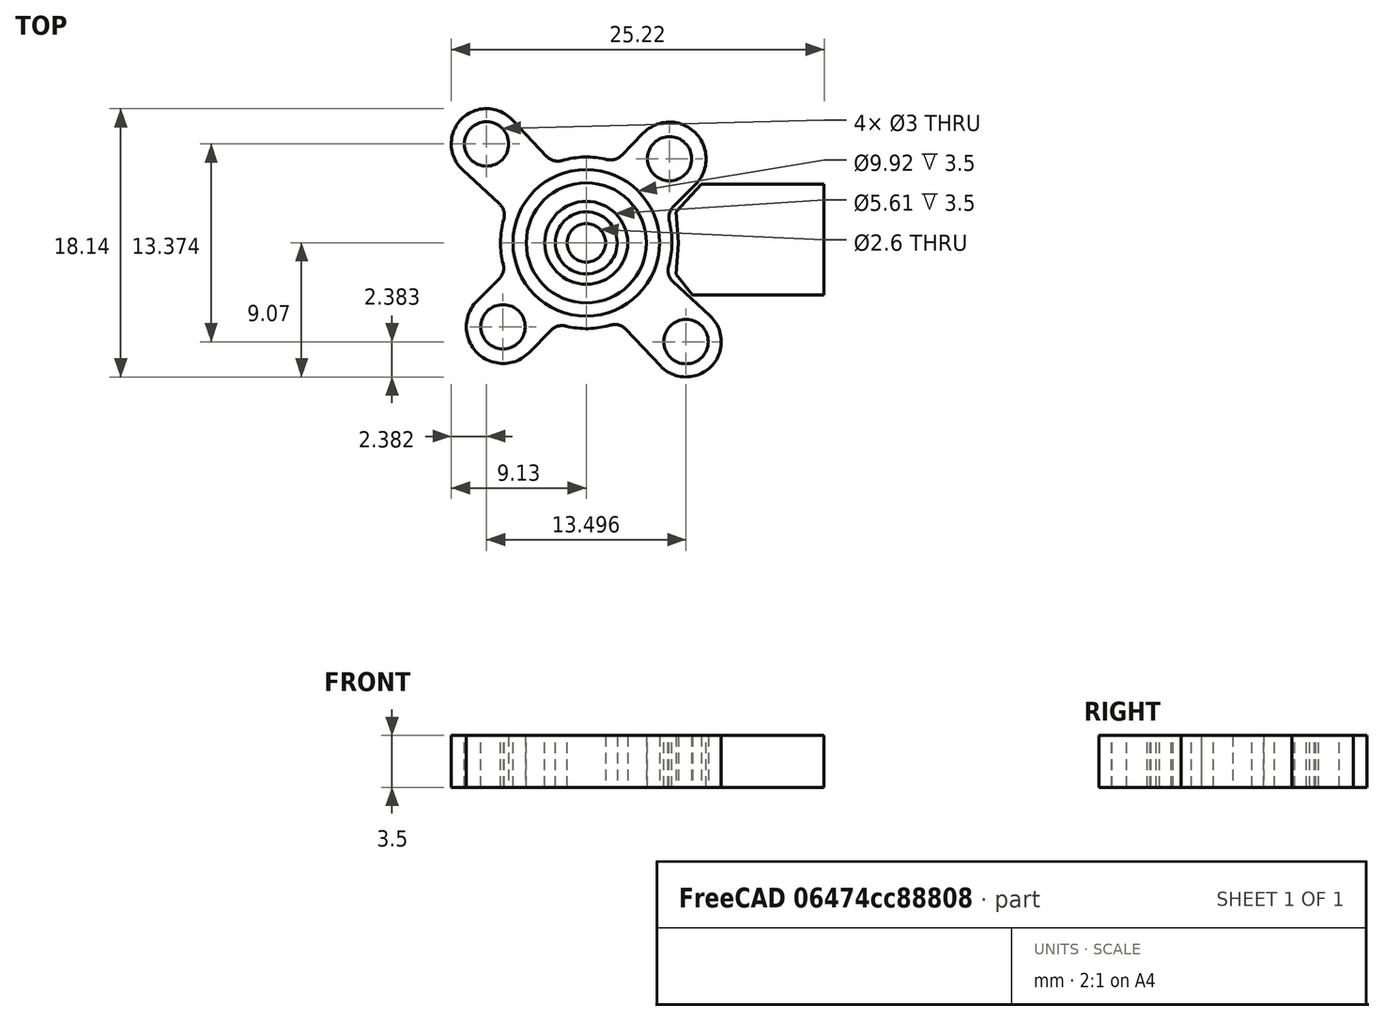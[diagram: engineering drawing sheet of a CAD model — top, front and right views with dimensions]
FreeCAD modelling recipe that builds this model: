
FCSTD DOCUMENT  (FreeCAD 0.18RUnknown)
Label: r6_bottom
License: All rights reserved
LicenseURL: http://en.wikipedia.org/wiki/All_rights_reserved
objects: Sketcher::SketchObject×2, Part::Extrusion×1
note: 3 computed .brp shape members not serialized (recipe doc carries the construction recipe); baked Part::Feature solids carry a one-line shape summary decoded from their .brp

FEATURE [Sketcher::SketchObject] Sketch  label="body"
  Placement = pos=(0,0,0) rot=(1,0,0;1.5708rad)
  sketch-geometry (23):
    g0: LineSegment StartX=-14 StartY=0 StartZ=0 EndX=14 EndY=0 EndZ=0
    g1: LineSegment StartX=14 StartY=0 StartZ=0 EndX=14 EndY=7.7 EndZ=0
    g2: LineSegment StartX=14 StartY=7.7 StartZ=0 EndX=-14 EndY=7.7 EndZ=0
    g3: LineSegment StartX=-14 StartY=0 StartZ=0 EndX=-14 EndY=7.7 EndZ=0
    g4: LineSegment StartX=-5.833 StartY=13.25 StartZ=0 EndX=5.833 EndY=13.25 EndZ=0
    g5: LineSegment StartX=-2.5 StartY=13.25 StartZ=0 EndX=-2.5 EndY=18.25 EndZ=0
    g6: LineSegment StartX=-2.5 StartY=18.25 StartZ=0 EndX=2.5 EndY=18.25 EndZ=0
    g7: LineSegment StartX=2.5 StartY=18.25 StartZ=0 EndX=2.5 EndY=13.25 EndZ=0
    g8: LineSegment StartX=-2.5 StartY=18.25 StartZ=0 EndX=-2.5 EndY=25.25 EndZ=0
    g9: LineSegment StartX=-2.5 StartY=25.25 StartZ=0 EndX=2.5 EndY=25.25 EndZ=0
    g10: LineSegment StartX=2.5 StartY=25.25 StartZ=0 EndX=2.5 EndY=18.25 EndZ=0
    g11: LineSegment StartX=-5.175 StartY=0 StartZ=0 EndX=-5.75 EndY=-2 EndZ=0
    g12: LineSegment StartX=5.175 StartY=0 StartZ=0 EndX=5.75 EndY=-2 EndZ=0
    g13: LineSegment StartX=-5.75 StartY=-2 StartZ=0 EndX=5.75 EndY=-2 EndZ=0
    g14: GeomPoint X=0 Y=-5.45 Z=0
    g15: GeomPoint X=0 Y=25.25 Z=0
    g16: GeomPoint X=0 Y=13.25 Z=0
    g17: GeomPoint X=10.0114 Y=8.91857 Z=0
    g18: LineSegment StartX=14 StartY=7.7 StartZ=0 EndX=14 EndY=9.64 EndZ=0
    g19: LineSegment StartX=14 StartY=9.64 StartZ=0 EndX=5.833 EndY=13.25 EndZ=0
    g20: LineSegment StartX=-5.833 StartY=13.25 StartZ=0 EndX=-14 EndY=9.64 EndZ=0
    g21: LineSegment StartX=-14 StartY=7.7 StartZ=0 EndX=-14 EndY=9.64 EndZ=0
    g22: GeomPoint X=0 Y=7.7 Z=0
  constraints (62):
    c: PointOnObject(g0,g-1)
    c: Horizontal(g0)
    c: Vertical(g1)
    c: Horizontal(g2)
    c: Coincident(g3,g0)
    c: Coincident(g3,g2)
    c: Vertical(g3)
    c: Horizontal(g4)
    c: PointOnObject(g5,g4)
    c: Vertical(g5)
    c: Coincident(g6,g5)
    c: Horizontal(g6)
    c: Coincident(g7,g6)
    c: PointOnObject(g7,g4)
    c: Vertical(g7)
    c: Coincident(g8,g5)
    c: Vertical(g8)
    c: Horizontal(g9)
    c: Coincident(g10,g9)
    c: Coincident(g10,g6)
    c: Vertical(g10)
    c: PointOnObject(g11,g0)
    c: PointOnObject(g12,g0)
    c: Coincident(g13,g11)
    c: Horizontal(g13)
    c: Coincident(g12,g13)
    c: Coincident(g2,g1)
    c: DistanceY(g11,g11) = 2
    c: PointOnObject(g14,g-2)
    c: Equal(g11,g12)
    c: PointOnObject(g15,g9)
    c: PointOnObject(g16,g4)
    c: PointOnObject(g16,g-2)
    c: PointOnObject(g15,g-2)
    c: Coincident(g9,g8)
    c: DistanceY(g14,g16) = 18.7
    c: Coincident(g0,g1)
    c: DistanceY(g14,g15) = 30.7
    c: DistanceX(g8,g9) = 5
    c: DistanceY(g5,g8) = 7
    c: Symmetric(g8,g9,g-2)
    c: Symmetric(g4,g4,g-2)
    c: DistanceX(g2,g1) = 28
    c: Symmetric(g2,g1,g-2)
    c: DistanceY(g0,g1) = 7.7
    c: Coincident(g18,g1)
    c: Coincident(g19,g18)
    c: Coincident(g19,g4)
    c: Coincident(g20,g4)
    c: Coincident(g21,g2)
    c: Coincident(g21,g20)
    c: Vertical(g18)
    c: Equal(g18,g21)
    c: Equal(g19,g20)
    c: PointOnObject(g22,g2)
    c: PointOnObject(g22,g-2)
    c: DistanceY(g22,g16) = 5.55
    c: Symmetric(g11,g12,g-2)
    c: DistanceX(g11,g12) = 10.35
    c: DistanceY(g1,g18) = 1.94
    c: DistanceX(g11,g12) = 11.5
    c: DistanceX(g4,g4) = 11.666
FEATURE [Sketcher::SketchObject] Sketch001  label="base"
  sketch-geometry (51):
    g0: Circle CenterX=0 CenterY=0 CenterZ=0 NormalX=0 NormalY=0 NormalZ=1 AngleXU=0 Radius=4.95833
    g1: Circle CenterX=0 CenterY=0 CenterZ=0 NormalX=0 NormalY=0 NormalZ=1 AngleXU=0 Radius=4.05855
    g2: Circle CenterX=0 CenterY=0 CenterZ=0 NormalX=0 NormalY=0 NormalZ=1 AngleXU=0 Radius=2.80253
    g3: Circle CenterX=0 CenterY=0 CenterZ=0 NormalX=0 NormalY=0 NormalZ=1 AngleXU=0 Radius=2.09587
    g4: Circle CenterX=0 CenterY=0 CenterZ=0 NormalX=0 NormalY=0 NormalZ=1 AngleXU=0 Radius=1.30129
    g5: ArcOfCircle CenterX=6.748 CenterY=6.68689 CenterZ=0 NormalX=0 NormalY=0 NormalZ=1 AngleXU=0 Radius=2.38428 StartAngle=5.45879 EndAngle=8.66928
    g6: ArcOfCircle CenterX=5.63107 CenterY=-5.68252 CenterZ=0 NormalX=0 NormalY=0 NormalZ=1 AngleXU=0 Radius=2.47766 StartAngle=3.91796 EndAngle=7.06852
    g7: ArcOfCircle CenterX=-6.748 CenterY=-6.68689 CenterZ=0 NormalX=0 NormalY=0 NormalZ=1 AngleXU=0 Radius=2.38428 StartAngle=2.3172 EndAngle=5.52769
    g8: ArcOfCircle CenterX=-5.63107 CenterY=5.68252 CenterZ=0 NormalX=0 NormalY=0 NormalZ=1 AngleXU=0 Radius=2.47766 StartAngle=0.776367 EndAngle=3.92693
    g9: ArcOfCircle CenterX=0 CenterY=0 CenterZ=0 NormalX=0 NormalY=0 NormalZ=1 AngleXU=0 Radius=5.8 StartAngle=1.28437 EndAngle=1.81386
    g10: ArcOfCircle CenterX=0 CenterY=0 CenterZ=0 NormalX=0 NormalY=0 NormalZ=1 AngleXU=0 Radius=5.8 StartAngle=6.03102 EndAngle=6.56052
    g11: ArcOfCircle CenterX=0 CenterY=0 CenterZ=0 NormalX=0 NormalY=0 NormalZ=1 AngleXU=0 Radius=5.8 StartAngle=2.88943 EndAngle=3.41892
    g12: ArcOfCircle CenterX=0 CenterY=0 CenterZ=0 NormalX=0 NormalY=0 NormalZ=1 AngleXU=0 Radius=5.8 StartAngle=4.42596 EndAngle=4.95546
    g13: ArcOfCircle CenterX=-1.9299 CenterY=-6.55258 CenterZ=0 NormalX=0 NormalY=0 NormalZ=1 AngleXU=0 Radius=1.03087 StartAngle=1.28437 EndAngle=2.3861
    g14: LineSegment StartX=-2.6803 StartY=-5.84576 StartZ=0 EndX=-5.0124 EndY=-8.32168 EndZ=0
    g15: ArcOfCircle CenterX=1.9299 CenterY=6.55258 CenterZ=0 NormalX=0 NormalY=0 NormalZ=1 AngleXU=0 Radius=1.03087 StartAngle=4.42596 EndAngle=5.52769
    g16: ArcOfCircle CenterX=6.56986 CenterY=1.87022 CenterZ=0 NormalX=0 NormalY=0 NormalZ=1 AngleXU=0 Radius=1.03087 StartAngle=2.3172 EndAngle=3.41892
    g17: ArcOfCircle CenterX=6.61484 CenterY=-1.70429 CenterZ=0 NormalX=0 NormalY=0 NormalZ=1 AngleXU=0 Radius=1.03087 StartAngle=2.88943 EndAngle=3.92693
    g18: ArcOfCircle CenterX=1.64406 CenterY=-6.63007 CenterZ=0 NormalX=0 NormalY=0 NormalZ=1 AngleXU=0 Radius=1.03087 StartAngle=0.776367 EndAngle=1.81386
    g19: ArcOfCircle CenterX=-6.56986 CenterY=-1.87022 CenterZ=0 NormalX=0 NormalY=0 NormalZ=1 AngleXU=0 Radius=1.03087 StartAngle=5.45879 EndAngle=6.56052
    g20: ArcOfCircle CenterX=-6.61484 CenterY=1.70429 CenterZ=0 NormalX=0 NormalY=0 NormalZ=1 AngleXU=0 Radius=1.03087 StartAngle=6.03102 EndAngle=7.06852
    g21: ArcOfCircle CenterX=-1.64406 CenterY=6.63007 CenterZ=0 NormalX=0 NormalY=0 NormalZ=1 AngleXU=0 Radius=1.03087 StartAngle=3.91796 EndAngle=4.95546
    g22: LineSegment StartX=-3.86335 StartY=7.4186 StartZ=0 EndX=-2.37954 EndY=5.90775 EndZ=0
    g23: LineSegment StartX=-5.88586 StartY=2.43318 StartZ=0 EndX=-7.38315 EndY=3.93067 EndZ=0
    g24: LineSegment StartX=-5.8699 StartY=-2.62702 StartZ=0 EndX=-8.36692 EndY=-4.93651 EndZ=0
    g25: LineSegment StartX=2.37954 StartY=-5.90775 StartZ=0 EndX=3.86335 EndY=-7.4186 EndZ=0
    g26: LineSegment StartX=7.38315 StartY=-3.93067 StartZ=0 EndX=5.88586 EndY=-2.43318 EndZ=0
    g27: LineSegment StartX=5.8699 StartY=2.62702 StartZ=0 EndX=8.36692 EndY=4.93651 EndZ=0
    g28: LineSegment StartX=2.6803 StartY=5.84576 StartZ=0 EndX=5.0124 EndY=8.32168 EndZ=0
    g29: Circle [constr] CenterX=0 CenterY=0 CenterZ=0 NormalX=0 NormalY=0 NormalZ=1 AngleXU=0 Radius=8
    g30: Circle [constr] CenterX=0 CenterY=0 CenterZ=0 NormalX=0 NormalY=0 NormalZ=1 AngleXU=0 Radius=9.5
    g31: Circle [constr] CenterX=0 CenterY=0 CenterZ=0 NormalX=0 NormalY=0 NormalZ=1 AngleXU=0 Radius=5.8
    g32: LineSegment [constr] StartX=-6.748 StartY=-6.68689 StartZ=0 EndX=6.748 EndY=6.68689 EndZ=0
    g33: LineSegment [constr] StartX=-5.63107 StartY=5.68252 StartZ=0 EndX=5.63107 EndY=-5.68252 EndZ=0
    g34: Circle CenterX=6.748 CenterY=6.68689 CenterZ=0 NormalX=0 NormalY=0 NormalZ=1 AngleXU=0 Radius=1.5
    g35: Circle CenterX=-5.63107 CenterY=5.68252 CenterZ=0 NormalX=0 NormalY=0 NormalZ=1 AngleXU=0 Radius=1.5
    g36: Circle CenterX=-6.748 CenterY=-6.68689 CenterZ=0 NormalX=0 NormalY=0 NormalZ=1 AngleXU=0 Radius=1.5
    g37: Circle CenterX=5.63107 CenterY=-5.68252 CenterZ=0 NormalX=0 NormalY=0 NormalZ=1 AngleXU=0 Radius=1.5
    g38: LineSegment StartX=16.0881 StartY=-3.97669 StartZ=0 EndX=16.0881 EndY=3.52014 EndZ=0
    g39: GeomPoint X=16.0952 Y=3.53033 Z=0
    g40: GeomPoint X=16.0881 Y=3.52014 Z=0
    g41: GeomPoint X=16.0952 Y=3.53033 Z=0
    g42: GeomPoint X=16.0881 Y=3.52014 Z=0
    g43: GeomPoint X=16.0952 Y=3.53033 Z=0
    g44: GeomPoint X=12.9914 Y=0 Z=0
    g45: LineSegment StartX=16.0881 StartY=3.52014 StartZ=0 EndX=7.18391 EndY=3.52014 EndZ=0
    g46: LineSegment StartX=7.18391 StartY=3.52014 StartZ=0 EndX=6.0724 EndY=2.14391 EndZ=0
    g47: LineSegment StartX=6.0724 StartY=2.14391 StartZ=0 EndX=6.22587 EndY=0 EndZ=0
    g48: LineSegment StartX=6.22587 StartY=0 StartZ=0 EndX=6.06438 EndY=-2.09343 EndZ=0
    g49: LineSegment StartX=6.06438 StartY=-2.09343 StartZ=0 EndX=7.79416 EndY=-3.97669 EndZ=0
    g50: LineSegment StartX=7.79416 StartY=-3.97669 StartZ=0 EndX=16.0881 EndY=-3.97669 EndZ=0
  constraints (115):
    c: Coincident(g0,g-1)
    c: Coincident(g2,g-1)
    c: Coincident(g3,g-1)
    c: Coincident(g4,g-1)
    c: Tangent(g14,g13) = -1.5708
    c: Tangent(g13,g12) = 1.5708
    c: Tangent(g14,g7) = 1.5708
    c: Coincident(g15,g9)
    c: Coincident(g16,g10)
    c: Coincident(g17,g10)
    c: Coincident(g18,g12)
    c: Coincident(g19,g11)
    c: Coincident(g20,g11)
    c: Coincident(g21,g9)
    c: Coincident(g22,g8)
    c: Coincident(g22,g21)
    c: Coincident(g23,g20)
    c: Coincident(g23,g8)
    c: Coincident(g24,g19)
    c: Coincident(g24,g7)
    c: Coincident(g25,g18)
    c: Coincident(g25,g6)
    c: Coincident(g26,g6)
    c: Coincident(g26,g17)
    c: Coincident(g27,g16)
    c: Coincident(g27,g5)
    c: Coincident(g28,g15)
    c: Coincident(g28,g5)
    c: Tangent(g28,g15)
    c: Tangent(g9,g15)
    c: Tangent(g28,g5)
    c: Tangent(g5,g27)
    c: Tangent(g16,g27)
    c: Tangent(g16,g10)
    c: Tangent(g10,g17)
    c: Tangent(g17,g26)
    c: Tangent(g26,g6)
    c: Tangent(g6,g25)
    c: Tangent(g25,g18)
    c: Tangent(g12,g18)
    c: Tangent(g7,g24)
    c: Tangent(g24,g19)
    c: Tangent(g19,g11)
    c: Tangent(g11,g20)
    c: Tangent(g20,g23)
    c: Tangent(g23,g8)
    c: Tangent(g22,g8)
    c: Tangent(g22,g21)
    c: Tangent(g9,g21)
    c: Coincident(g29,g-1)
    c: Coincident(g30,g-1)
    c: PointOnObject(g8,g29)
    c: PointOnObject(g5,g30)
    c: PointOnObject(g6,g29)
    c: PointOnObject(g7,g30)
    c: Coincident(g31,g-1)
    c: PointOnObject(g9,g31)
    c: PointOnObject(g9,g31)
    c: Radius(g29) = 8
    c: Radius(g30) = 9.5
    c: Radius(g31) = 5.8
    c: PointOnObject(g10,g31)
    c: PointOnObject(g12,g31)
    c: PointOnObject(g12,g31)
    c: PointOnObject(g10,g31)
    c: PointOnObject(g11,g31)
    c: PointOnObject(g11,g31)
    c: Equal(g5,g7)
    c: Equal(g8,g6)
    c: Equal(g13,g18)
    c: Equal(g13,g19)
    c: Equal(g20,g19)
    c: Equal(g21,g15)
    c: Equal(g21,g20)
    c: Equal(g15,g16)
    c: Equal(g17,g16)
    c: Equal(g11,g12)
    c: Equal(g12,g10)
    c: Equal(g10,g9)
    c: Equal(g22,g23)
    c: Equal(g22,g26)
    c: Equal(g26,g25)
    c: Equal(g14,g24)
    c: Equal(g28,g27)
    c: Equal(g28,g24)
    c: Coincident(g32,g7)
    c: PointOnObject(g-1,g32)
    c: Coincident(g1,g-1)
    c: PointOnObject(g10,g32)
    c: PointOnObject(g5,g32)
    c: Coincident(g32,g5)
    c: Coincident(g33,g8)
    c: Coincident(g33,g6)
    c: Angle(g33,g32) = 1.5708
    c: Coincident(g34,g5)
    c: Radius(g34) = 1.5
    c: Coincident(g35,g8)
    c: Coincident(g36,g7)
    c: Coincident(g37,g6)
    c: Equal(g34,g35)
    c: Equal(g35,g36)
    c: Equal(g36,g37)
    c: PointOnObject(g-1,g33)
    c: Vertical(g38)
    c: Coincident(g40,g38)
    c: Coincident(g42,g38)
    c: Coincident(g45,g38)
    c: Horizontal(g45)
    c: Coincident(g47,g46)
    c: Coincident(g48,g47)
    c: Coincident(g49,g48)
    c: Coincident(g50,g38)
    c: Horizontal(g50)
    c: Coincident(g50,g49)
    c: Coincident(g46,g45)
FEATURE [Part::Extrusion] Extrude
  Base = -> Sketch001
  Dir = (0,0,1)
  DirMode = 2
  FaceMakerClass = Part::FaceMakerBullseye
  LengthFwd = 3.5
  LengthRev = 0
  Placement = pos=(0,0,3.5) rot=(1,0,0;3.14159rad)
  Solid = true
  Symmetric = false
